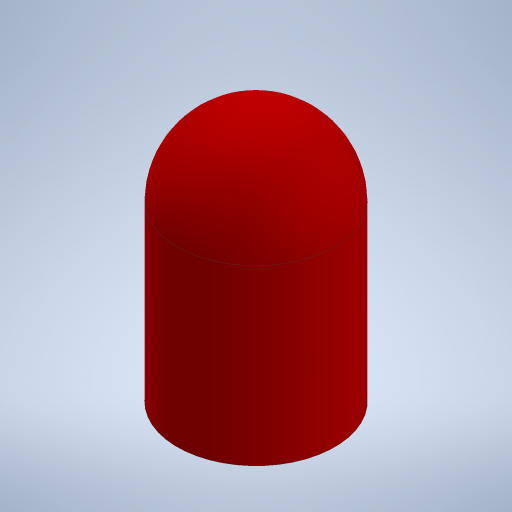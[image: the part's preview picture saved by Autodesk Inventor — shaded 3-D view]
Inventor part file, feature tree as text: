
AUTODESK INVENTOR PART (.ipt)
format: ipt  version: 2024.2 (Build 282272000, 272)  size: 239,104 bytes
history: native  units: mm
features: extrude x1, fillet x1, sketch x1
ambient origin geometry x8: Origin, YZ Plane, XZ Plane, XY Plane, X Axis, Y Axis, Z Axis, Center Point
bodies: Solid1 (feature_tree)
feature tree (3):
  extrude  "Extrusion1"  Depth=2.5mm TaperAngle=0.0deg
  fillet  "Fillet1"  Radius=2.5mm
  sketch  "Sketch1"  dims[d0=5.0mm d1=8.0mm d2=0.0mm d3=2.5mm]
